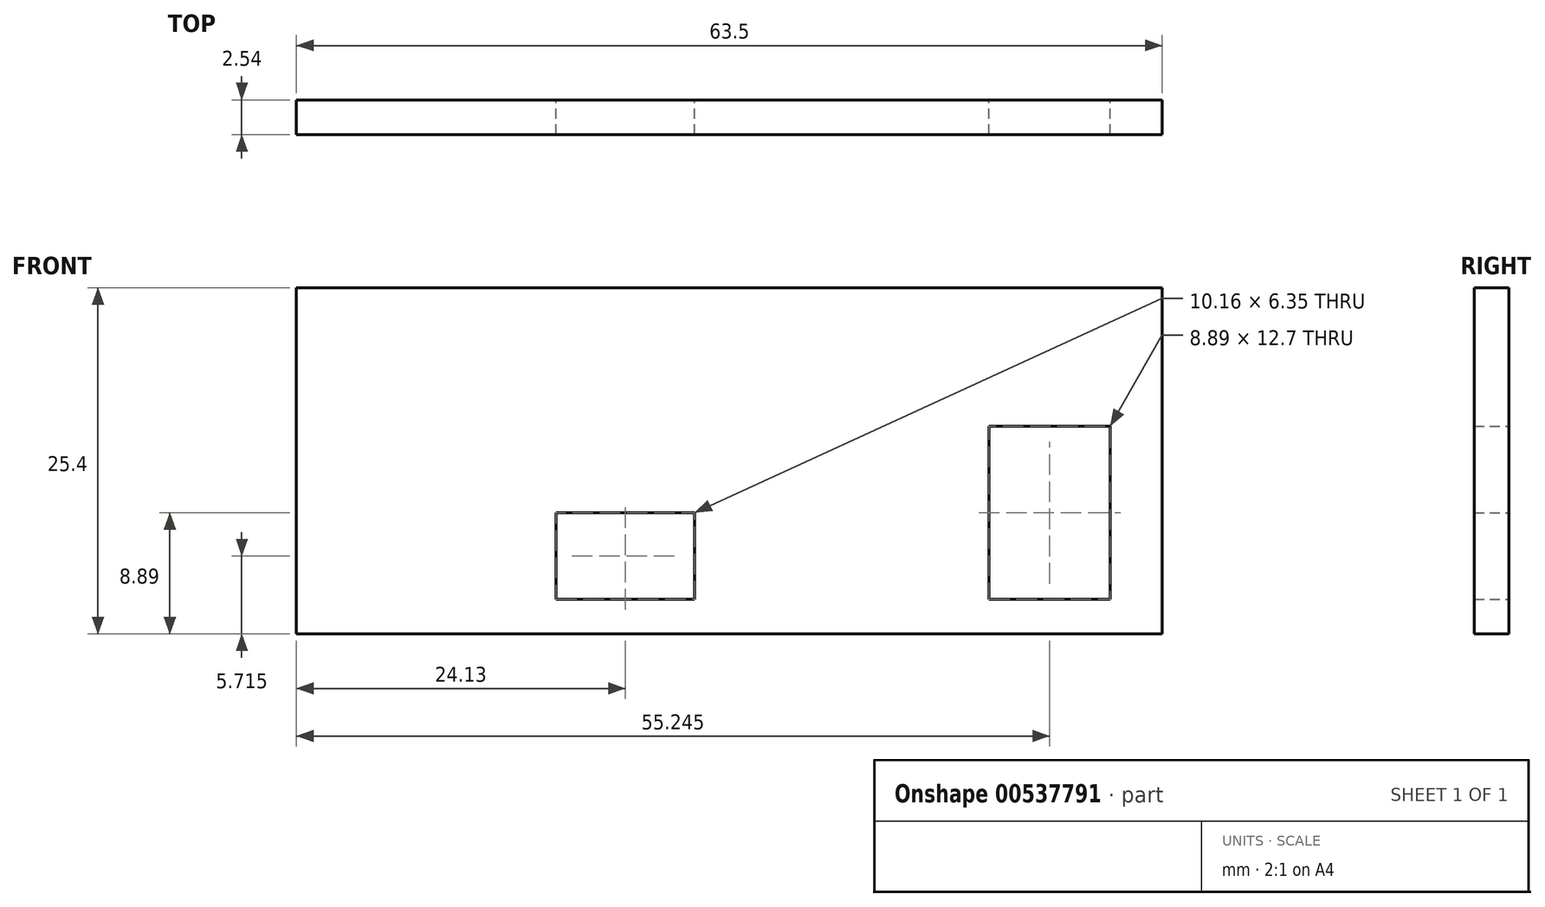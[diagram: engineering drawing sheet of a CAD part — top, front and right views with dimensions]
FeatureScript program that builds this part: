
annotation { "Feature Type Name" : "Feature", "Feature Type Description" : "" }
export const myFeature = defineFeature(function(context is Context, id is Id, definition is map)
    precondition{}
    {
        {
            var Q0;
            Q0=qCreatedBy(makeId("Front.planeOp"),FACE);
            var sketch = newSketch(context, id + "F0", { "sketchPlane" : qUnion([Q0])});
            skLineSegment(sketch, "E0.bottom", {"start": v(0, -15.24) * mm, "end": v(-63.5, -15.24) * mm});
            skLineSegment(sketch, "E0.top", {"start": v(0, 10.16) * mm, "end": v(-63.5, 10.16) * mm});
            skLineSegment(sketch, "E0.left", {"start": v(0, -15.24) * mm, "end": v(0, 10.16) * mm});
            skLineSegment(sketch, "E0.right", {"start": v(-63.5, -15.24) * mm, "end": v(-63.5, 10.16) * mm});
            skLineSegment(sketch, "E1.bottom", {"start": v(-3.8, -12.7) * mm, "end": v(-12.7, -12.7) * mm});
            skLineSegment(sketch, "E1.top", {"start": v(-3.8, 0) * mm, "end": v(-12.7, 0) * mm});
            skLineSegment(sketch, "E1.left", {"start": v(-3.8, -12.7) * mm, "end": v(-3.8, 0) * mm});
            skLineSegment(sketch, "E1.right", {"start": v(-12.7, -12.7) * mm, "end": v(-12.7, 0) * mm});
            skLineSegment(sketch, "E2.bottom", {"start": v(-44.45, -6.35) * mm, "end": v(-34.29, -6.35) * mm});
            skLineSegment(sketch, "E2.top", {"start": v(-44.45, -12.7) * mm, "end": v(-34.29, -12.7) * mm});
            skLineSegment(sketch, "E2.left", {"start": v(-44.45, -6.35) * mm, "end": v(-44.45, -12.7) * mm});
            skLineSegment(sketch, "E2.right", {"start": v(-34.29, -6.35) * mm, "end": v(-34.29, -12.7) * mm});
            skSolve(sketch);
        }
        {
            var Q0;
            Q0=makeQuery(id+"F0.imprint","IMPRINT",FACE,{"disambiguationData":[TD([[makeQuery(id+"F0.imprint","IMPRINT",EDGE,{"derivedFrom":sQuery(id+"F0.wireOp",EDGE,"E0.bottom")}),-1.0]])]});
            extrude(context, id + "F1", {"entities" : qUnion([Q0]), "endBound" : BoundingType.SYMMETRIC, "depth" : 2.54 * mm, "offsetDistance" : 25.4 * mm});
        }
    });
